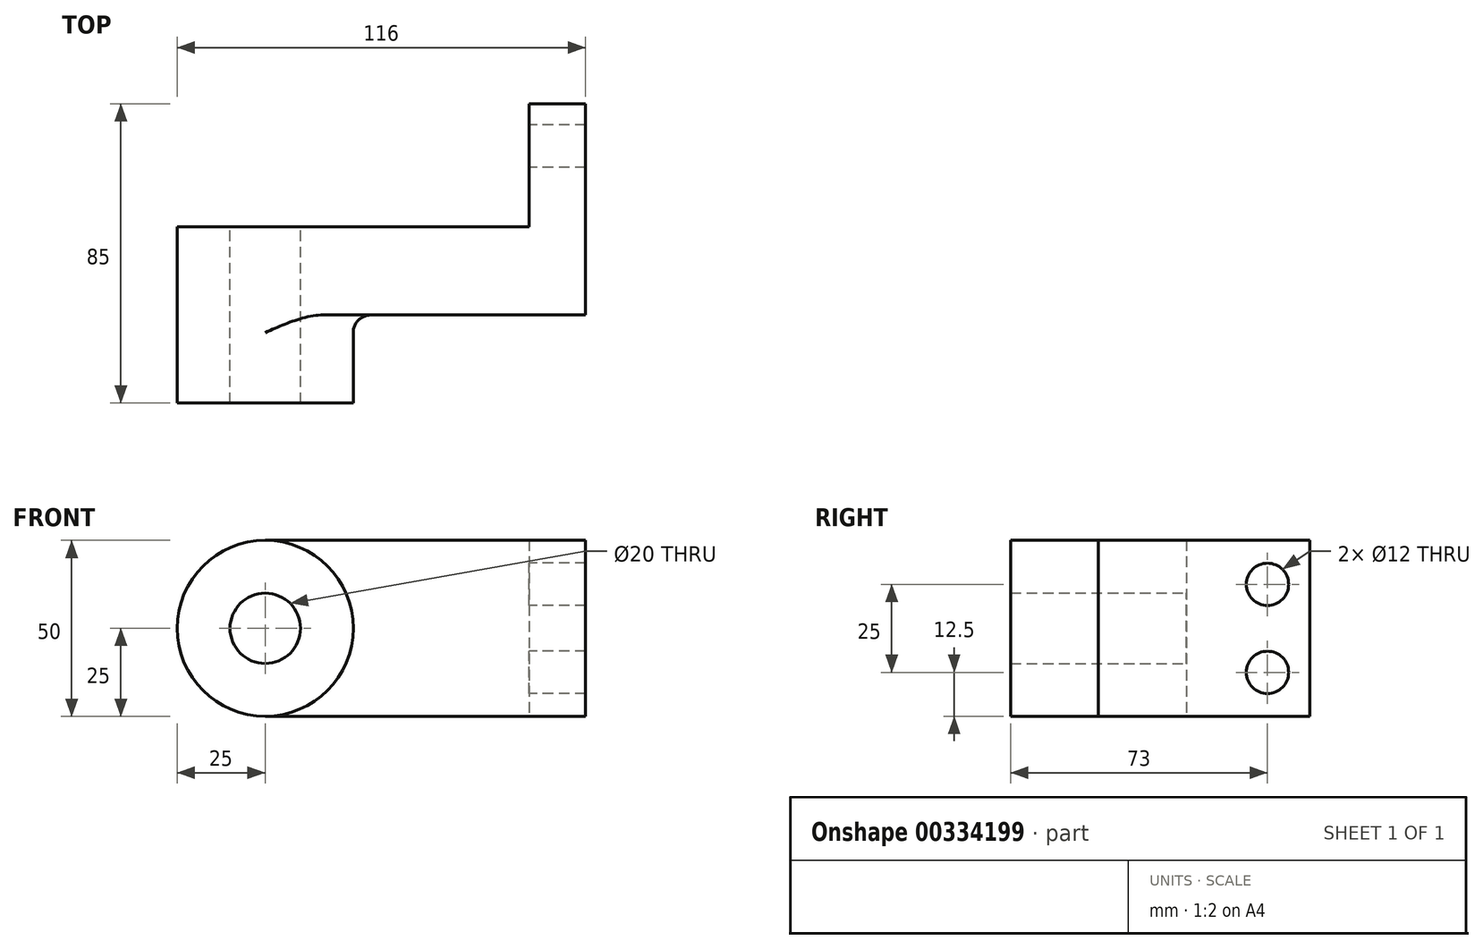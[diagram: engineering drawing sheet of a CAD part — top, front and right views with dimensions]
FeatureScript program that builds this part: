
annotation { "Feature Type Name" : "Feature", "Feature Type Description" : "" }
export const myFeature = defineFeature(function(context is Context, id is Id, definition is map)
    precondition{}
    {
        {
            var Q0;
            Q0=qCreatedBy(makeId("Front.planeOp"),FACE);
            var sketch = newSketch(context, id + "F0", { "sketchPlane" : qUnion([Q0])});
            skLineSegment(sketch, "E0.bottom", {"start": v(37.5, 25) * mm, "end": v(-37.5, 25) * mm});
            skLineSegment(sketch, "E0.top", {"start": v(37.5, -25) * mm, "end": v(-37.5, -25) * mm});
            skLineSegment(sketch, "E0.left", {"start": v(37.5, 25) * mm, "end": v(37.5, -25) * mm});
            skLineSegment(sketch, "E0.right", {"start": v(-37.5, 25) * mm, "end": v(-37.5, -25) * mm});
            skPoint(sketch, "E0.middle", {"position": v(0, 0) * mm});
            skCircle(sketch, "E1", {"center": v(-37.5, 0) * mm, "radius": 25 * mm});
            skPoint(sketch, "E1.centerSnap0", {"position": v(-37.5, 0) * mm});
            skCircle(sketch, "E2", {"center": v(-37.5, 0) * mm, "radius": 10 * mm});
            skSolve(sketch);
        }
        {
            var Q0;
            {var subQ0=sQuery(id+"F0.wireOp",EDGE,"E0.bottom");Q0=makeQuery(id+"F0.imprint","IMPRINT",FACE,{"disambiguationData":[TD([[makeQuery(id+"F0.imprint","IMPRINT",EDGE,{"derivedFrom":subQ0}),1.0]])]});}
            var Q1;
            {var subQ1=sQuery(id+"F0.wireOp",EDGE,"E0.right");var subQ3=sQuery(id+"F0.wireOp",EDGE,"E2");var subQ4=makeQuery(id+"F0.imprint","INTERSECT",VERTEX,{"disambiguationData":[OD(0.0)],"derivedFrom":[subQ1,subQ3]});Q1=makeQuery(id+"F0.imprint","IMPRINT",FACE,{"disambiguationData":[TD([[makeQuery(id+"F0.imprint","IMPRINT",EDGE,{"disambiguationData":[TD([[subQ4,-1.0]])],"derivedFrom":subQ3}),-1.0]])]});}
            var Q2;
            {var subQ1=sQuery(id+"F0.wireOp",EDGE,"E0.right");var subQ3=sQuery(id+"F0.wireOp",EDGE,"E2");var subQ4=makeQuery(id+"F0.imprint","INTERSECT",VERTEX,{"disambiguationData":[OD(0.0)],"derivedFrom":[subQ1,subQ3]});Q2=makeQuery(id+"F0.imprint","IMPRINT",FACE,{"disambiguationData":[TD([[makeQuery(id+"F0.imprint","IMPRINT",EDGE,{"disambiguationData":[TD([[subQ4,1.0]])],"derivedFrom":subQ3}),-1.0]])]});}
            extrude(context, id + "F1", {"entities" : qUnion([Q0, Q1, Q2]), "depth" : 25 * mm});
        }
        {
            var Q0;
            {var subQ1=sQuery(id+"F0.wireOp",EDGE,"E0.right");var subQ3=sQuery(id+"F0.wireOp",EDGE,"E2");var subQ4=makeQuery(id+"F0.imprint","INTERSECT",VERTEX,{"disambiguationData":[OD(0.0)],"derivedFrom":[subQ1,subQ3]});Q0=makeQuery(id+"F0.imprint","IMPRINT",FACE,{"disambiguationData":[TD([[makeQuery(id+"F0.imprint","IMPRINT",EDGE,{"disambiguationData":[TD([[subQ4,1.0]])],"derivedFrom":subQ3}),-1.0]])]});}
            var Q1;
            {var subQ1=sQuery(id+"F0.wireOp",EDGE,"E0.right");var subQ3=sQuery(id+"F0.wireOp",EDGE,"E2");var subQ4=makeQuery(id+"F0.imprint","INTERSECT",VERTEX,{"disambiguationData":[OD(0.0)],"derivedFrom":[subQ1,subQ3]});Q1=makeQuery(id+"F0.imprint","IMPRINT",FACE,{"disambiguationData":[TD([[makeQuery(id+"F0.imprint","IMPRINT",EDGE,{"disambiguationData":[TD([[subQ4,-1.0]])],"derivedFrom":subQ3}),-1.0]])]});}
            extrude(context, id + "F2", {"entities" : qUnion([Q0, Q1]), "operationType" : NewBodyOperationType.ADD, "depth" : 50 * mm});
        }
        {
            var Q0;
            Q0=makeQuery(id+"F1.opExtrude","SWEPT_FACE",FACE,{"disambiguationData":[OSD([sQuery(id+"F0.wireOp",EDGE,"E0.left")])]});
            var sketch = newSketch(context, id + "F3", { "sketchPlane" : qUnion([Q0])});
            skLineSegment(sketch, "E3.bottom", {"start": v(-25, -25) * mm, "end": v(35, -25) * mm});
            skLineSegment(sketch, "E3.top", {"start": v(-25, 25) * mm, "end": v(35, 25) * mm});
            skLineSegment(sketch, "E3.left", {"start": v(-25, -25) * mm, "end": v(-25, 25) * mm});
            skLineSegment(sketch, "E3.right", {"start": v(35, -25) * mm, "end": v(35, 25) * mm});
            skCircle(sketch, "E4", {"center": v(23, 12.5) * mm, "radius": 6 * mm});
            skCircle(sketch, "E5.MirrorC", {"center": v(23, -12.5) * mm, "radius": 6 * mm});
            skSolve(sketch);
        }
        {
            var Q0;
            {var subQ2=sQuery(id+"F3.wireOp",EDGE,"E3.right");Q0=makeQuery(id+"F3.imprint","IMPRINT",FACE,{"disambiguationData":[TD([[makeQuery(id+"F3.imprint","IMPRINT",EDGE,{"derivedFrom":subQ2}),1.0]])]});}
            var Q1;
            {var subQ2=sQuery(id+"F3.wireOp",EDGE,"E3.left");Q1=makeQuery(id+"F3.imprint","IMPRINT",FACE,{"disambiguationData":[TD([[makeQuery(id+"F3.imprint","IMPRINT",EDGE,{"derivedFrom":subQ2}),1.0]])]});}
            extrude(context, id + "F4", {"entities" : qUnion([Q0, Q1]), "operationType" : NewBodyOperationType.ADD, "depth" : 16 * mm});
        }
        {
            var Q0;
            Q0=makeQuery(id+"F1.opExtrude","CAP_EDGE",EDGE,{"disambiguationData":[OSD([sQuery(id+"F0.wireOp",EDGE,"E0.left")])],"isStart":true});
            var Q1;
            {var subQ0=sQuery(id+"F0.wireOp",EDGE,"E1");Q1=makeQuery(id+"F2.boolean.opBoolean","INTERSECT",EDGE,{"derivedFrom":[makeQuery(id+"F1.opExtrude","CAP_FACE",FACE,{"disambiguationData":[OSD([sQuery(id+"F0.wireOp",EDGE,"E0.bottom"),sQuery(id+"F0.wireOp",EDGE,"E0.top"),sQuery(id+"F0.wireOp",EDGE,"E0.left"),subQ0,sQuery(id+"F0.wireOp",EDGE,"E2")])],"isStart":false}),makeQuery(id+"F2.opExtrude","SWEPT_FACE",FACE,{"disambiguationData":[OSD([subQ0])]})]});}
            fillet(context, id + "F5", {"entities" : qUnion([Q0, Q1]), "radius" : 5 * mm, "tangentPropagation" : true, "allowEdgeOverflow" : false});
        }
    });
